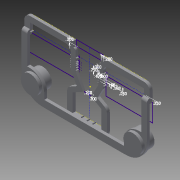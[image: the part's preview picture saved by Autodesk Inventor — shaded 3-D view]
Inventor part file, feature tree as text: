
AUTODESK INVENTOR PART (.ipt)
format: ipt  version: 2015 SP1 (Build 190203100, 203)  size: 620,032 bytes
history: native  units: in
note: dims shown in document units (in); Inventor stores cm internally (conversion verified against a paired STEP export)
features: extrude x10, sketch x8, fillet x7, projected_geometry x2
ambient origin geometry x8: Origin, YZ Plane, XZ Plane, XY Plane, X Axis, Y Axis, Z Axis, Center Point
bodies: Solid1 (feature_tree)
feature tree (27):
  extrude  "Extrusion1"  Depth=11.0in
  extrude  "Extrusion2"  Depth=0.5in
  extrude  "Extrusion3"  Depth=0.4in
  sketch  "Sketch4"  dims[d13=0.4in d14=0.5in d15=0.4in]
  extrude  "Extrusion5"  Depth=0.5in
  fillet  "Fillet1"  Radius=0.4in
  sketch  "Sketch6"  dims[d18=0.5in d19=0.5in]
  extrude  "Extrusion6"  Depth=0.4in
  sketch  "Sketch7"  dims[d20=0.25in d21=0.0in d24=0.6in]
  extrude  "Extrusion11"  Depth=0.5in
  sketch  "Sketch8"  dims[d25=1.03in d28=4.5in d34=3.5in d35=0.25in d36=0.0in d37=0.3in d38=0.3in d39=0.25in d40=0.0in d42=0.1in d47=0.6in d48=0.0in d49=0.5in d51=0.05in d52=0.1in d67=0.05in d68=0.1in d83=0.25in d84=0.0in d97=0.75in d98=1.0in d99=1.25in d100=1.0in d101=1.25in d102=0.5in d105=0.2in d106=0.4in d107=0.25in d108=0.0in d109=0.2in d110=0.2in d111=0.0in d112=0.05in d113=0.0in d114=0.05in d115=0.0in d116=0.5in d117=0.2in d119=0.5in d120=0.5in d121=1.0in d124=3.5in d133=0.05in d134=0.6in d136=0.1875in d137=0.1875in d138=0.125in d139=0.125in d140=0.25in d141=0.0in d142=1.0in d143=1.5in d144=2.1in d146=0.025in d147=0.1in d148=0.25in d149=0.0in d150=0.2in d151=1.25in d152=2.25in d153=3.0in d155=1.7in d156=0.1in d157=0.05in d158=1.0in d159=0.0in d160=0.75in d161=0.25in d162=0.25in d163=0.7874in d165=0.5in d166=0.7874in d168=0.5in]
  extrude  "Extrusion15"  Depth=0.25in
  extrude  "Extrusion14"  Depth=0.25in
  extrude  "Extrusion12"  Depth=0.25in
  extrude  "Extrusion13"  Depth=0.25in TaperAngle=0.0deg
  fillet  "Fillet4"  Radius=0.3in
  fillet  "Fillet5"  Radius=0.3in
  fillet  "Fillet7"  Radius=0.25in
  fillet  "Fillet8"  Radius=0.1in
  fillet  "Fillet10"  Radius=0.6in
  fillet  "Fillet11"  Radius=0.5in
  sketch  "Sketch1"  dims[d2=3.5in d4=11.0in]
  sketch  "Sketch2"  dims[d8=3.0in d10=0.5in]
  sketch  "Sketch3"  dims[d11=0.4in d12=0.4in]
  sketch  "Sketch5"  dims[d16=0.4in d17=0.4in]
  projected_geometry  "Projected Loop1"
  projected_geometry  "Project Cut Edges1"
